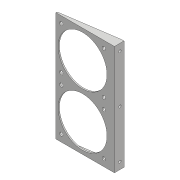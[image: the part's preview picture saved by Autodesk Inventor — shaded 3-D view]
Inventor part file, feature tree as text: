
AUTODESK INVENTOR PART (.ipt)
format: ipt  version: 2018 (Build 220112000, 112)  size: 154,112 bytes
history: native  units: mm
features: sketch x5, extrude x4, mirror x2, hole x2, projected_geometry x2
ambient origin geometry x8: Origin, YZ Plane, XZ Plane, XY Plane, X Axis, Y Axis, Z Axis, Center Point
bodies: Solid1 (feature_tree)
feature tree (15):
  extrude  "Extrusion1"  Depth=100.0mm
  extrude  "Extrusion2"  Depth=9.0mm
  extrude  "Extrusion3"  Depth=1.5mm TaperAngle=0.0deg
  mirror  "Mirror1"
  hole  "Hole1"  [1 undecoded]
  sketch  "Sketch5"  dims[d10=2.4mm d11=6.0mm d12=4.4mm d13=2.0mm d14=90.0deg d15=8.0mm d16=20.594885mm d17=46.0mm d18=40.0mm d19=40.0mm d20=25.0mm d21=25.0mm d22=10.0mm d23=0.0mm d24=3.2mm d25=6.0mm d26=6.3mm d27=2.0mm d28=90.0deg d29=8.0mm d30=20.594885mm]
  extrude  "Extrusion4"  Depth=2.0mm
  hole  "Hole2"  [1 undecoded]
  mirror  "Mirror2"
  sketch  "Sketch1"  dims[d0=53.0mm d1=100.0mm]
  sketch  "Sketch2"  dims[d2=1.2mm d3=0.0mm d4=9.0mm]
  sketch  "Sketch3"  dims[d5=2.0mm d6=0.0mm d7=1.5mm d8=0.0mm]
  projected_geometry  "Projected Loop1"
  sketch  "Sketch4"  dims[d9=90.0mm]
  projected_geometry  "Projected Loop2"
note: 2 required parameter values undecoded (feature->parameter linkage not recoverable at this tier; creation-order binding heuristic only, values carry confidence <= 0.55)
